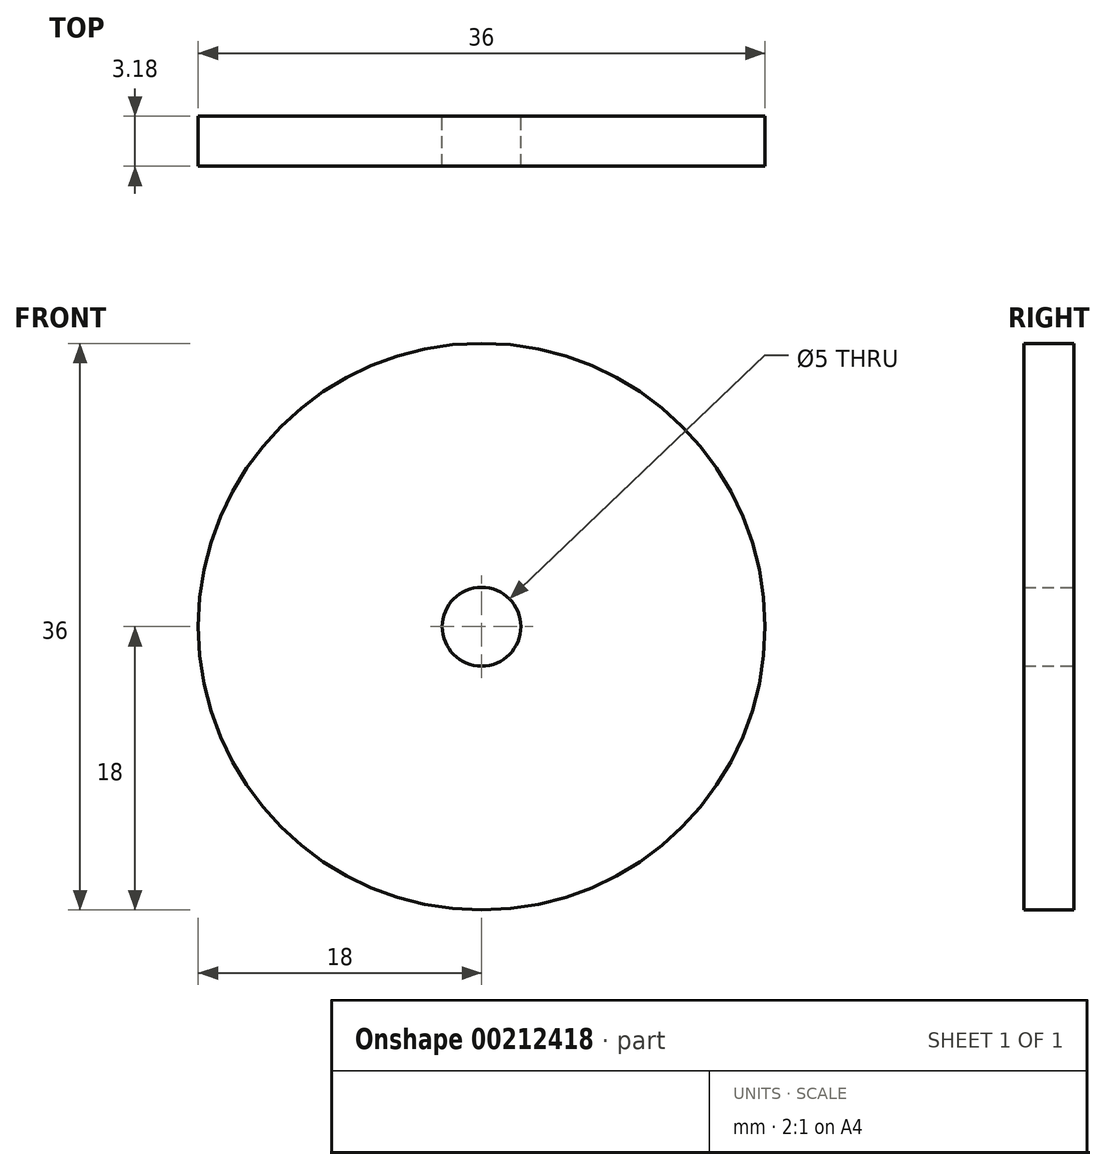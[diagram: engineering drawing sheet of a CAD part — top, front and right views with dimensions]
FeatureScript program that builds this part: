
annotation { "Feature Type Name" : "Feature", "Feature Type Description" : "" }
export const myFeature = defineFeature(function(context is Context, id is Id, definition is map)
    precondition{}
    {
        {
            var Q0;
            Q0=qCreatedBy(makeId("Front.planeOp"),FACE);
            var sketch = newSketch(context, id + "F0", { "sketchPlane" : qUnion([Q0])});
            skCircle(sketch, "E0", {"center": v(0, 0) * mm, "radius": 18 * mm});
            skCircle(sketch, "E1", {"center": v(0, 0) * mm, "radius": 2.5 * mm});
            skSolve(sketch);
        }
        {
            var Q0;
            Q0=makeQuery(id+"F0.imprint","IMPRINT",FACE,{"disambiguationData":[TD([[makeQuery(id+"F0.imprint","IMPRINT",EDGE,{"derivedFrom":sQuery(id+"F0.wireOp",EDGE,"E0")}),1.0]])]});
            extrude(context, id + "F1", {"entities" : qUnion([Q0]), "depth" : 3.17 * mm});
        }
    });
